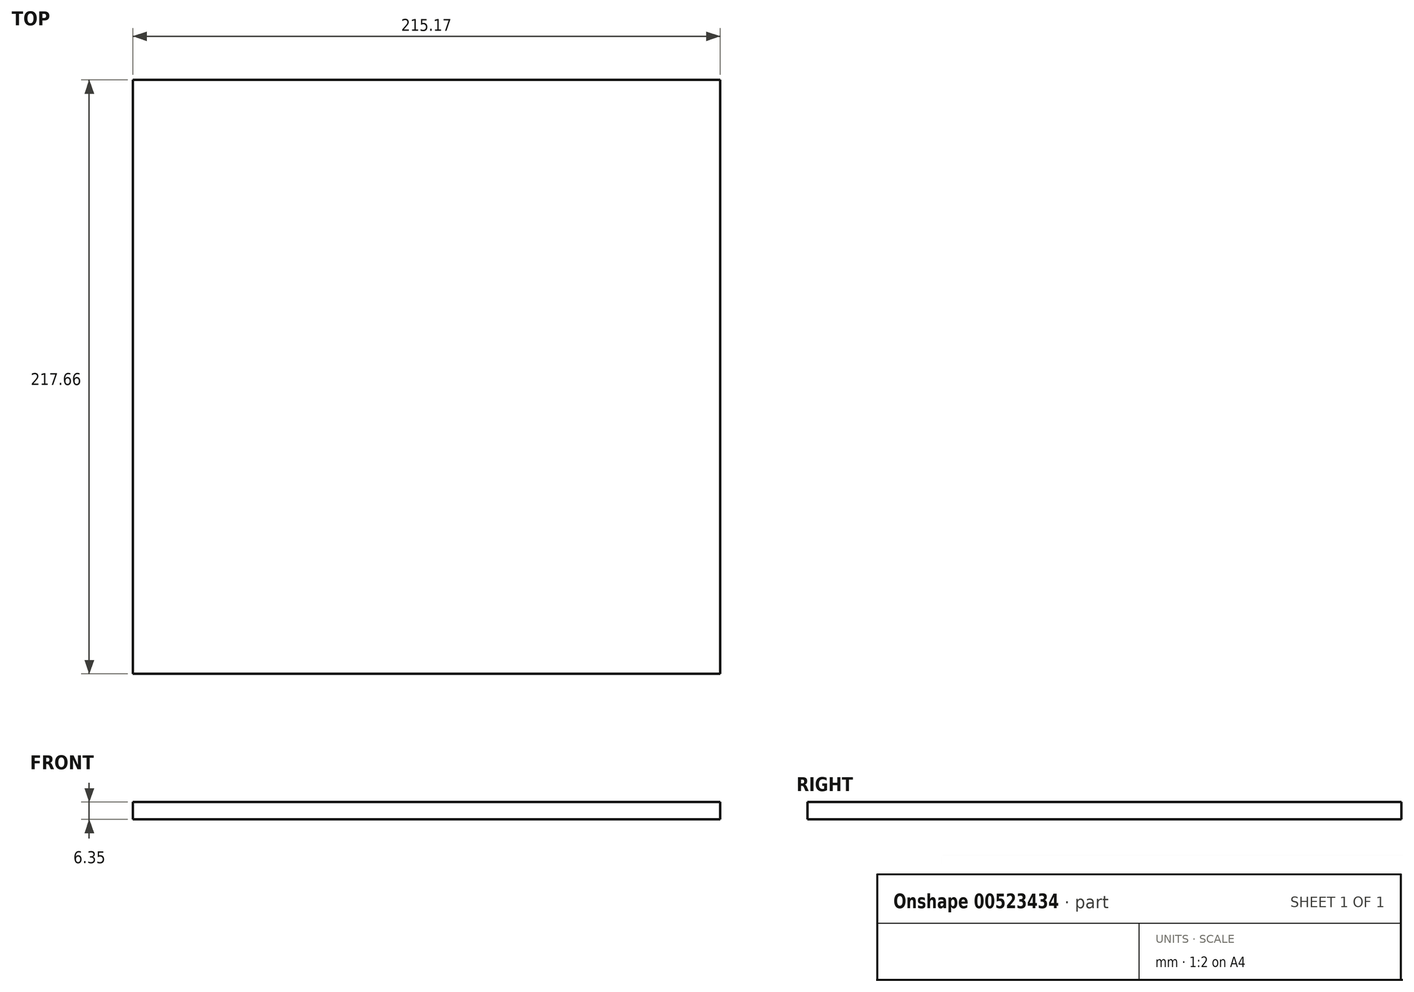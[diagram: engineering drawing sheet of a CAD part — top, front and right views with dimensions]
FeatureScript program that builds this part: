
annotation { "Feature Type Name" : "Feature", "Feature Type Description" : "" }
export const myFeature = defineFeature(function(context is Context, id is Id, definition is map)
    precondition{}
    {
        {
            var Q0;
            Q0=qCreatedBy(makeId("Top.planeOp"),FACE);
            var sketch = newSketch(context, id + "F0", { "sketchPlane" : qUnion([Q0])});
            skLineSegment(sketch, "E0.bottom", {"start": v(-101.32, 128.45) * mm, "end": v(113.85, 128.45) * mm});
            skLineSegment(sketch, "E0.top", {"start": v(-101.32, -89.21) * mm, "end": v(113.85, -89.21) * mm});
            skLineSegment(sketch, "E0.left", {"start": v(-101.32, 128.45) * mm, "end": v(-101.32, -89.21) * mm});
            skLineSegment(sketch, "E0.right", {"start": v(113.85, 128.45) * mm, "end": v(113.85, -89.21) * mm});
            skSolve(sketch);
        }
        {
            var Q0;
            Q0 = qSketchRegion(id + "F0", true);
            extrude(context, id + "F1", {"entities" : qUnion([Q0]), "depth" : 6.35 * mm, "offsetDistance" : 25.4 * mm});
        }
        {
            var Q0;
            Q0=makeQuery(id+"F1.opExtrude","CAP_FACE",FACE,{"disambiguationData":[OSD([sQuery(id+"F0.wireOp",EDGE,"E0.bottom"),sQuery(id+"F0.wireOp",EDGE,"E0.top"),sQuery(id+"F0.wireOp",EDGE,"E0.left"),sQuery(id+"F0.wireOp",EDGE,"E0.right")])],"isStart":false});
            var sketch = newSketch(context, id + "F2", { "sketchPlane" : qUnion([Q0])});
            skLineSegment(sketch, "E1.bottom", {"start": v(-35.62, 62.49) * mm, "end": v(68.04, 62.49) * mm});
            skLineSegment(sketch, "E1.top", {"start": v(-35.62, -37.96) * mm, "end": v(68.04, -37.96) * mm});
            skLineSegment(sketch, "E1.left", {"start": v(-35.62, 62.49) * mm, "end": v(-35.62, -37.96) * mm});
            skLineSegment(sketch, "E1.right", {"start": v(68.04, 62.49) * mm, "end": v(68.04, -37.96) * mm});
            skSolve(sketch);
        }
        {
            var Q0;
            Q0=sQuery(id+"F2.wireOp",EDGE,"E1.left");
            var Q1;
            Q1=sQuery(id+"F2.wireOp",EDGE,"E1.bottom");
            var Q2;
            Q2=sQuery(id+"F2.wireOp",EDGE,"E1.top");
            var Q3;
            Q3=sQuery(id+"F2.wireOp",EDGE,"E1.right");
            extrude(context, id + "F3", {"bodyType" : ToolBodyType.SURFACE, "surfaceEntities" : qUnion([Q0, Q1, Q2, Q3]), "depth" : 19.05 * mm, "offsetDistance" : 25.4 * mm});
        }
        {
            var Q0;
            Q0=makeQuery(id+"F1.opExtrude","CAP_FACE",FACE,{"disambiguationData":[OSD([sQuery(id+"F0.wireOp",EDGE,"E0.bottom"),sQuery(id+"F0.wireOp",EDGE,"E0.top"),sQuery(id+"F0.wireOp",EDGE,"E0.left"),sQuery(id+"F0.wireOp",EDGE,"E0.right")])],"isStart":false});
            var sketch = newSketch(context, id + "F4", { "sketchPlane" : qUnion([Q0])});
            skLineSegment(sketch, "E2", {"start": v(6.26, -86.05) * mm, "end": v(6.26, 13.52) * mm});
            skPoint(sketch, "E2.startSnap0", {"position": v(6.26, -89.21) * mm});
            skSolve(sketch);
        }
        {
            var Q0;
            Q0=sQuery(id+"F4.wireOp",EDGE,"E2");
            extrude(context, id + "F5", {"bodyType" : ToolBodyType.SURFACE, "surfaceEntities" : qUnion([Q0]), "depth" : 19.05 * mm, "offsetDistance" : 25.4 * mm});
        }
    });
